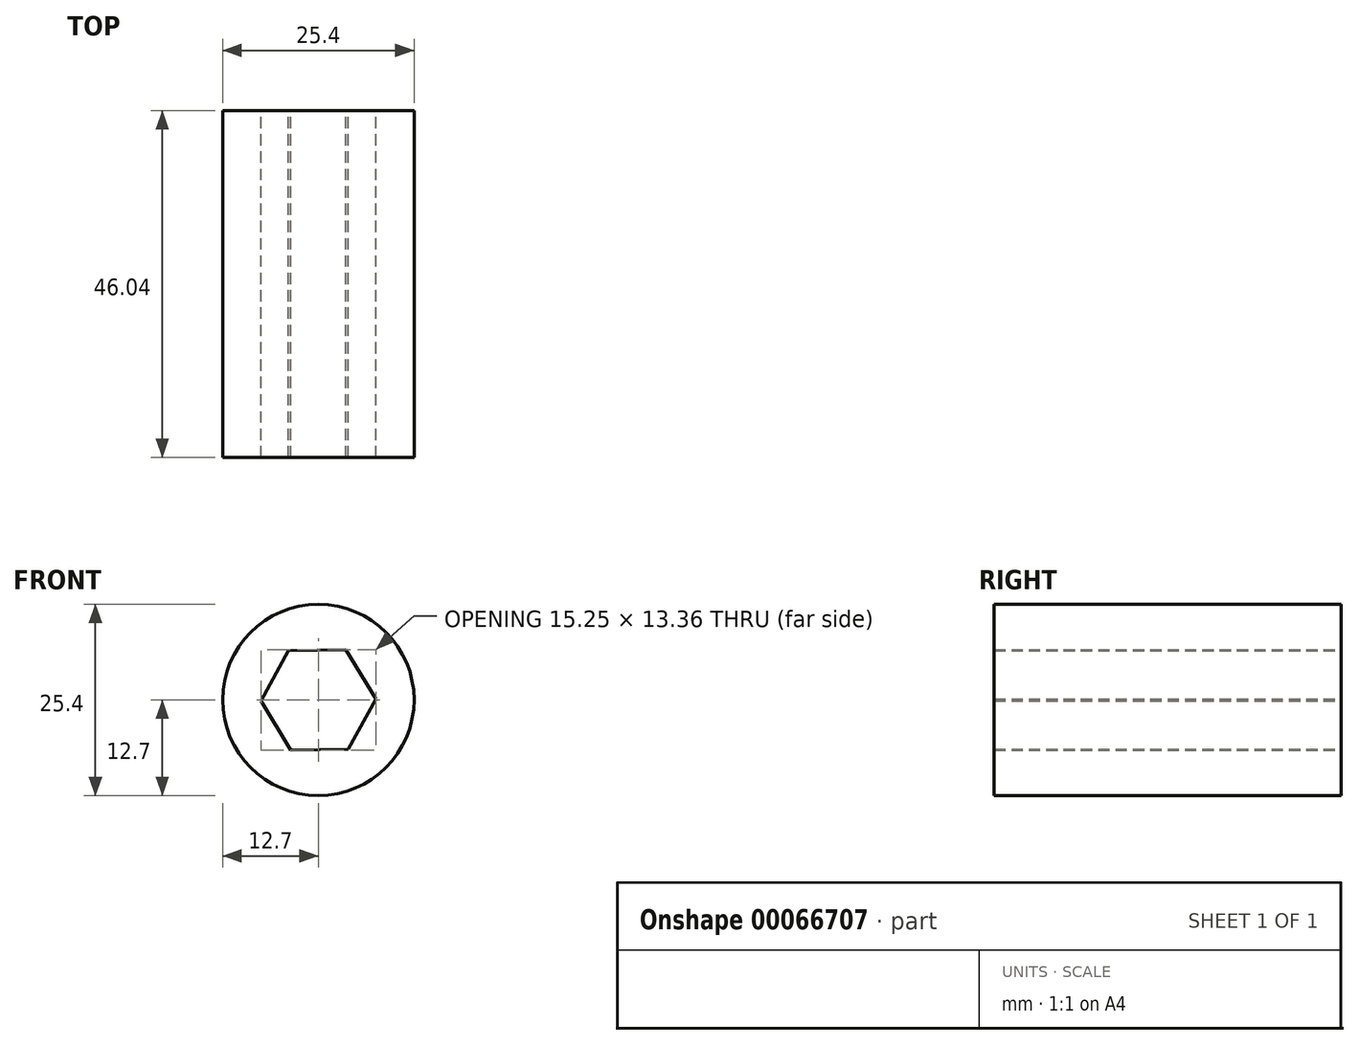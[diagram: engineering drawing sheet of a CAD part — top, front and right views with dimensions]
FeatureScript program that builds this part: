
annotation { "Feature Type Name" : "Feature", "Feature Type Description" : "" }
export const myFeature = defineFeature(function(context is Context, id is Id, definition is map)
    precondition{}
    {
        {
            var Q0;
            Q0=qCreatedBy(makeId("Front.planeOp"),FACE);
            var sketch = newSketch(context, id + "F0", { "sketchPlane" : qUnion([Q0])});
            skCircle(sketch, "E0", {"center": v(0, 0) * mm, "radius": 12.7 * mm});
            skCircle(sketch, "E1.cCircle", {"center": v(0, 0) * mm, "radius": 7.63 * mm, "construction": true});
            skLineSegment(sketch, "E1.0", {"start": v(3.68, 6.68) * mm, "end": v(7.62, 0.15) * mm});
            skLineSegment(sketch, "E1.1", {"start": v(7.62, 0.15) * mm, "end": v(3.95, -6.53) * mm});
            skLineSegment(sketch, "E1.2", {"start": v(3.95, -6.53) * mm, "end": v(-3.68, -6.68) * mm});
            skLineSegment(sketch, "E1.3", {"start": v(-3.68, -6.68) * mm, "end": v(-7.62, -0.15) * mm});
            skLineSegment(sketch, "E1.4", {"start": v(-7.62, -0.15) * mm, "end": v(-3.95, 6.53) * mm});
            skLineSegment(sketch, "E1.5", {"start": v(-3.95, 6.53) * mm, "end": v(3.68, 6.68) * mm});
            skSolve(sketch);
        }
        {
            var Q0;
            Q0=makeQuery(id+"F0.imprint","IMPRINT",FACE,{"disambiguationData":[TD([[makeQuery(id+"F0.imprint","IMPRINT",EDGE,{"derivedFrom":sQuery(id+"F0.wireOp",EDGE,"E0")}),1.0]])]});
            extrude(context, id + "F1", {"entities" : qUnion([Q0]), "depth" : 46.04 * mm});
        }
    });
